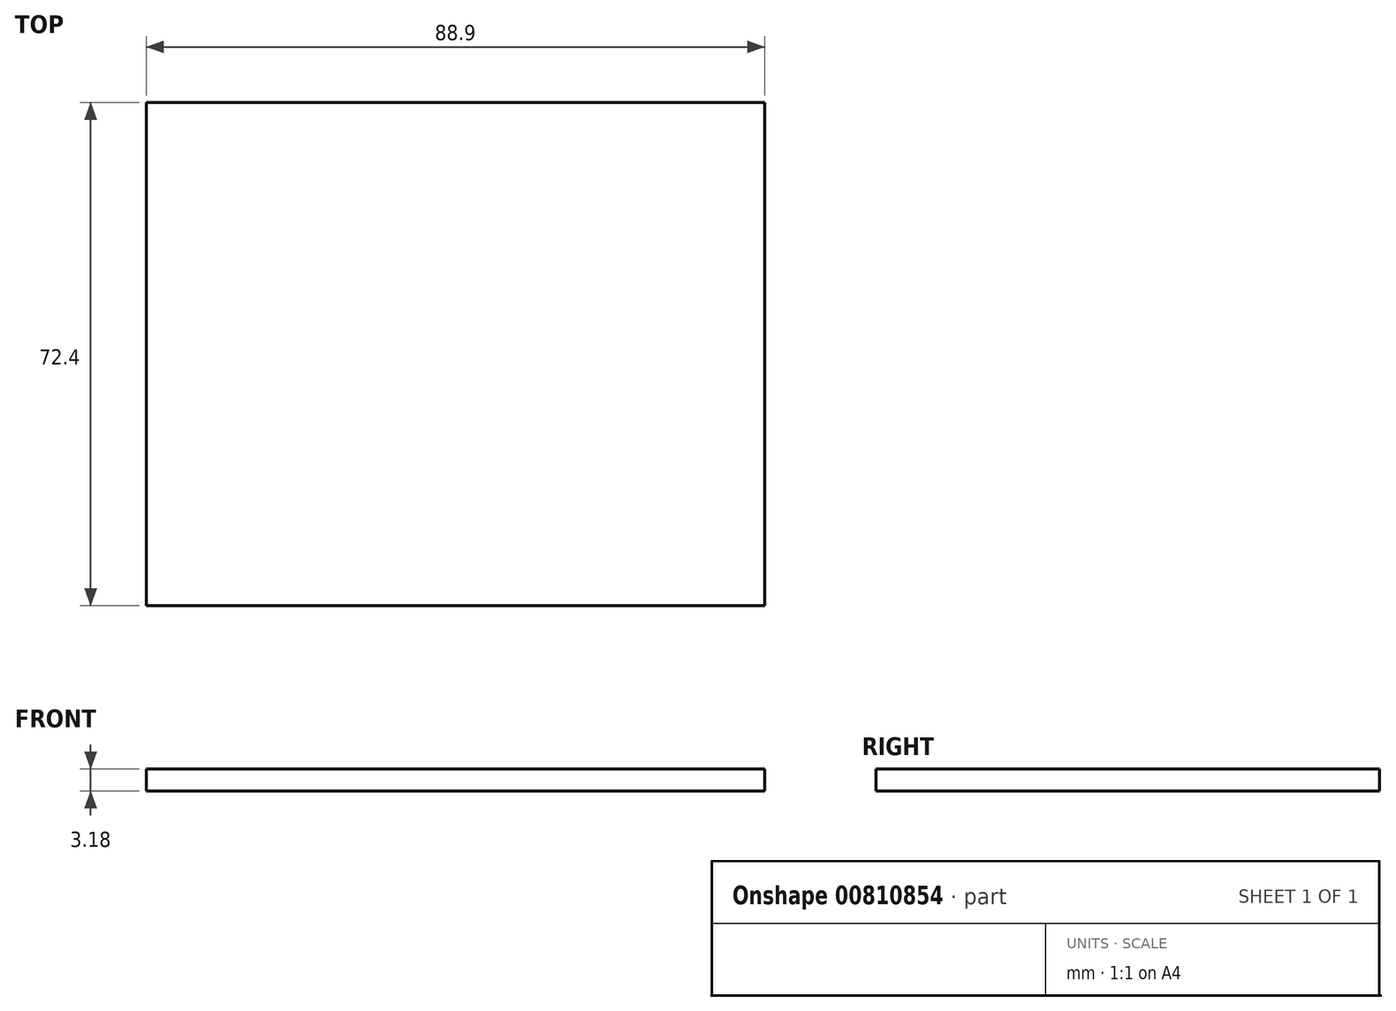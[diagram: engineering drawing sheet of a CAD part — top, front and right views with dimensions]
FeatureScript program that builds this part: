
annotation { "Feature Type Name" : "Feature", "Feature Type Description" : "" }
export const myFeature = defineFeature(function(context is Context, id is Id, definition is map)
    precondition{}
    {
        {
            var Q0;
            Q0=qCreatedBy(makeId("Right.planeOp"),FACE);
            var sketch = newSketch(context, id + "F0", { "sketchPlane" : qUnion([Q0])});
            skLineSegment(sketch, "E0.bottom", {"start": v(36.2, 1.59) * mm, "end": v(-36.2, 1.59) * mm});
            skLineSegment(sketch, "E0.top", {"start": v(36.2, -1.59) * mm, "end": v(-36.2, -1.59) * mm});
            skLineSegment(sketch, "E0.left", {"start": v(36.2, 1.59) * mm, "end": v(36.2, -1.59) * mm});
            skLineSegment(sketch, "E0.right", {"start": v(-36.2, 1.59) * mm, "end": v(-36.2, -1.59) * mm});
            skPoint(sketch, "E0.middle", {"position": v(0, 0) * mm});
            skSolve(sketch);
        }
        {
            var Q0;
            Q0=makeQuery(id+"F0.imprint","IMPRINT",FACE,{"disambiguationData":[TD([[makeQuery(id+"F0.imprint","IMPRINT",EDGE,{"derivedFrom":sQuery(id+"F0.wireOp",EDGE,"E0.bottom")}),1.0]])]});
            extrude(context, id + "F1", {"entities" : qUnion([Q0]), "depth" : 88.9 * mm, "offsetDistance" : 25.4 * mm});
        }
    });
